# Revit family: Kawneer_Window_GT70s_Pos0011
name_source: partatom
category: Windows
units: mm (PartAtom-declared; Revit-internal decimal feet)

## family parameters
Always vertical = Yes
Cut with Voids When Loaded = No
Host = Wall
OmniClass Number = 23.30.20.00
OmniClass Title = Windows
Room Calculation Point = No
Shared = No

## types (1)
- 1000mm(w)x1000mm(h)
    Assembly Code = B2020100
    AssetType = Fixed
    BIMObjectName = Kawneer_Window_GT70s_Pos001
    BottomPanel = 600 mm
    ClassificationName = Uniclass2015
    ClassificationValue = Pr_30_59_98_02
    Default Cill Height = 800 mm
    Description = Window
    DocumentationLiterature = https://www.kawneer.com
    DurationUnit = Years
    ExpectedLife = 0
    Finish = PPC
    FrameDepth = 72 mm  [stored 0.23622 ft]
    FrameWidth = 79 mm
    GlassOffset_EXT = 7 mm  [stored 0.0229659 ft]
    GlassThickness = 6 mm  [stored 0.019685 ft]
    GlazingThickness = 28 mm  [stored 0.0918635 ft]
    HeadTolerance = 0 mm  [stored 0 ft]
    Height = 1000 mm  [stored 3.28084 ft]
    IfcExportAs = IfcWindow
    IfcExportType = IfcWindowTypeEnum.WINDOW
    InternalRevealThickness = 5 mm  [stored 0.0164042 ft]
    JambTolerance = 0 mm  [stored 0 ft]
    Keynote = L10/330
    Manufacturer = Kawneer UK Limited
    ManufacturerName = Kawneer UK Limited
    Material = Aluminium
    Model = GT70s - Pos 001
    ModelNumber = GT70s - Pos 001
    ModelReference = 1000mm(w)x1000mm(h)
    NBSDescription = Aluminium window units
    NBSObjectName = Kawneer - Aluminium window units
    NBSReference = 45-25-99/310
    NominalDepth = 72 mm  [stored 0.23622 ft]
    NominalHeight = 1000 mm  [stored 3.28084 ft]
    NominalLength = 1000 mm  [stored 3.28084 ft]
    ProductionYear = 2022
    Rough Height = 1000 mm  [stored 3.28084 ft]
    Rough Width = 1000 mm  [stored 3.28084 ft]
    Shape = Rectangle
    Size = 1000mm(w)x1000mm(h)
    TopPanel = 600 mm
    Type Comments = 1000mm(w)x1000mm(h)
    TypeName = GT70s - Pos 001
    URL = https://www.kawneer.com
    Wall Closure = By host
    WarrantyDescription = Kawneer Lifetime Guarantee
    WarrantyDurationUnit = Years
    Width = 1000 mm  [stored 3.28084 ft]
    _BSBibleVersion = 16
    _BimSpecGuid = 0
    _CurrentRevision = 1
    _DistributedBy = www.bimstore.co.uk
    _ObjectUserGuide = www.bimstore.co.uk

note: [stored X ft] marks values corroborated as IEEE doubles in the binary element streams (Revit-internal decimal feet)

## geometry (parser evidence)
native form markers: Sweep x6
no freeform markers — native parametric forms only
